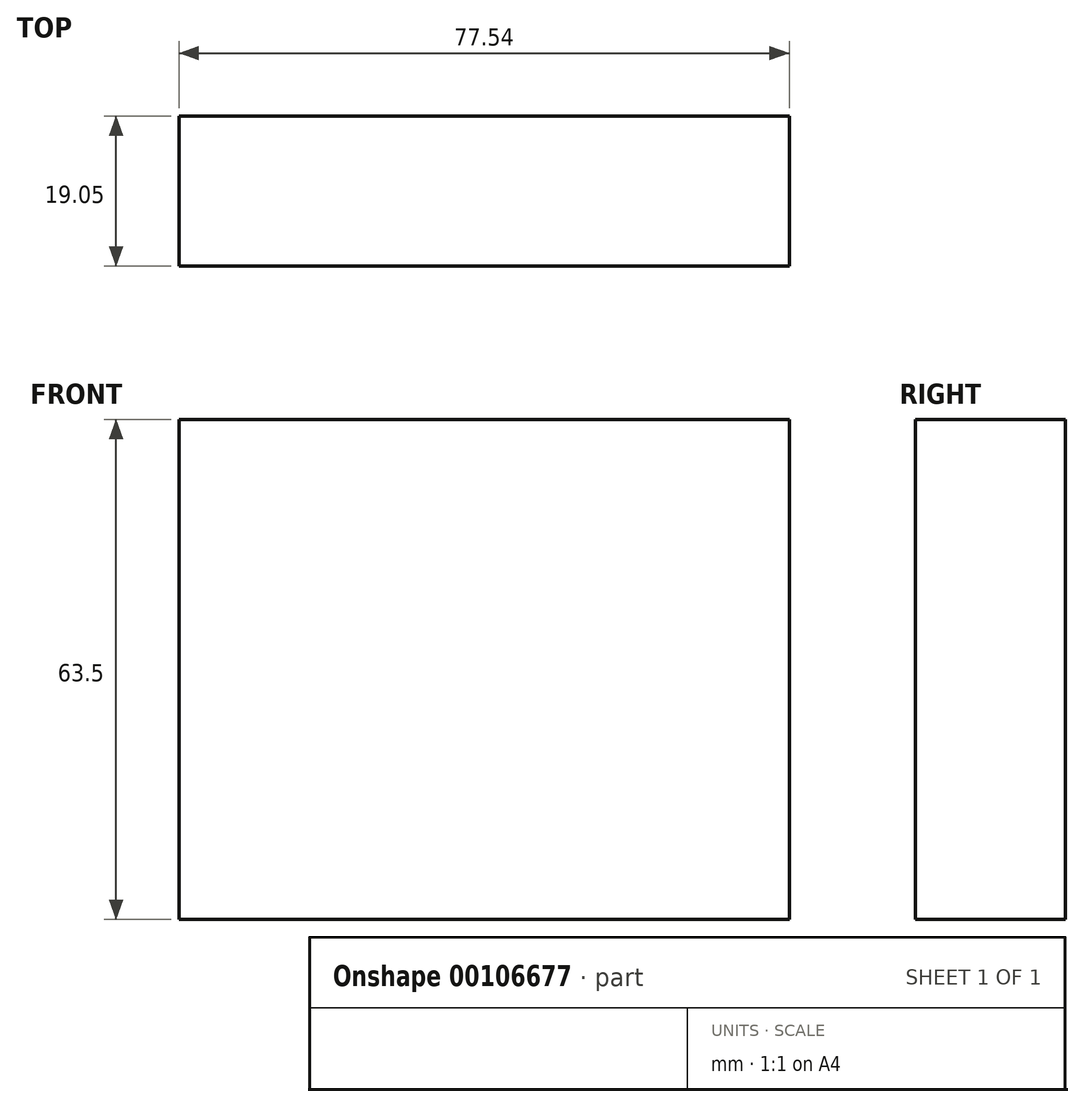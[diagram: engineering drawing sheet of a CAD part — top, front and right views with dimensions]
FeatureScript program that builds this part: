
annotation { "Feature Type Name" : "Feature", "Feature Type Description" : "" }
export const myFeature = defineFeature(function(context is Context, id is Id, definition is map)
    precondition{}
    {
        {
            var Q0;
            Q0=qCreatedBy(makeId("Front.planeOp"),FACE);
            var sketch = newSketch(context, id + "F0", { "sketchPlane" : qUnion([Q0])});
            skLineSegment(sketch, "E0.bottom", {"start": v(0, 0) * mm, "end": v(77.54, 0) * mm});
            skLineSegment(sketch, "E0.top", {"start": v(0, 63.5) * mm, "end": v(77.54, 63.5) * mm});
            skLineSegment(sketch, "E0.left", {"start": v(0, 0) * mm, "end": v(0, 63.5) * mm});
            skLineSegment(sketch, "E0.right", {"start": v(77.54, 0) * mm, "end": v(77.54, 63.5) * mm});
            skSolve(sketch);
        }
        {
            var Q0;
            Q0=makeQuery(id+"F0.imprint","IMPRINT",FACE,{"disambiguationData":[TD([[makeQuery(id+"F0.imprint","IMPRINT",EDGE,{"derivedFrom":sQuery(id+"F0.wireOp",EDGE,"E0.bottom")}),1.0]])]});
            extrude(context, id + "F1", {"entities" : qUnion([Q0]), "depth" : 19.05 * mm});
        }
    });
